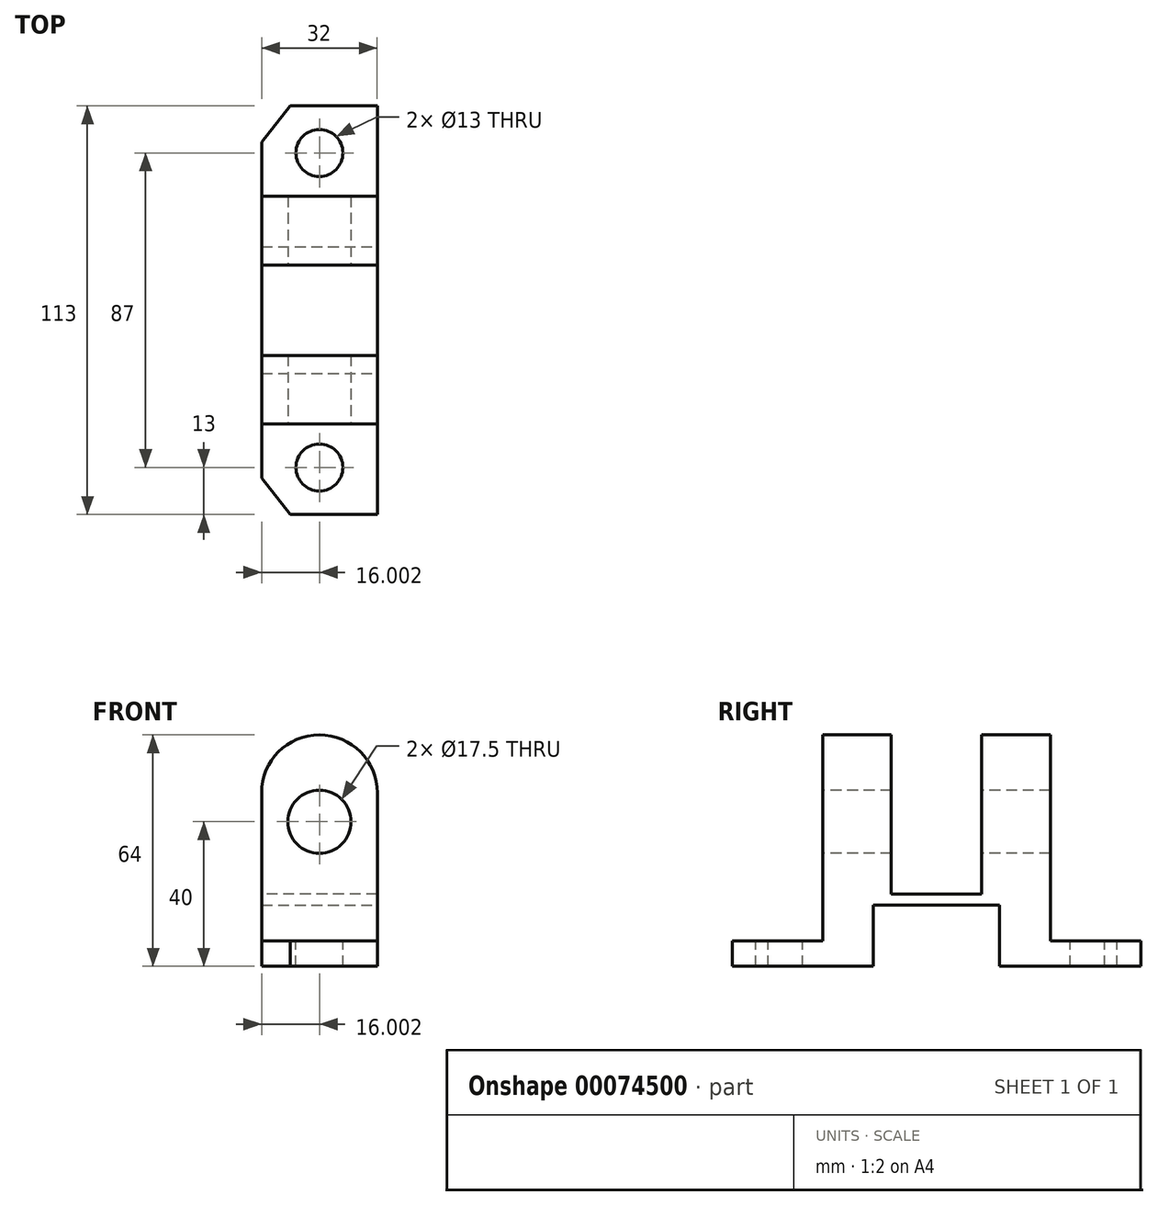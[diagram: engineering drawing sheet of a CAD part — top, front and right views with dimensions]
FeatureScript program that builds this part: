
annotation { "Feature Type Name" : "Feature", "Feature Type Description" : "" }
export const myFeature = defineFeature(function(context is Context, id is Id, definition is map)
    precondition{}
    {
        {
            var Q0;
            Q0=qCreatedBy(makeId("Top.planeOp"),FACE);
            var sketch = newSketch(context, id + "F0", { "sketchPlane" : qUnion([Q0])});
            skLineSegment(sketch, "E0.bottom", {"start": v(-7.48, 89.64) * mm, "end": v(-39.48, 89.64) * mm});
            skLineSegment(sketch, "E0.top", {"start": v(-7.48, -23.36) * mm, "end": v(-39.48, -23.36) * mm});
            skLineSegment(sketch, "E0.left", {"start": v(-7.48, 89.64) * mm, "end": v(-7.48, -23.36) * mm});
            skLineSegment(sketch, "E0.right", {"start": v(-39.48, 89.64) * mm, "end": v(-39.48, -23.36) * mm});
            skSolve(sketch);
        }
        {
            var Q0;
            Q0 = qSketchRegion(id + "F0", true);
            extrude(context, id + "F1", {"entities" : qUnion([Q0]), "depth" : 20 * mm});
        }
        {
            var Q0;
            Q0=makeQuery(id+"F1.opExtrude","CAP_FACE",FACE,{"disambiguationData":[OSD([sQuery(id+"F0.wireOp",EDGE,"E0.bottom"),sQuery(id+"F0.wireOp",EDGE,"E0.top"),sQuery(id+"F0.wireOp",EDGE,"E0.left"),sQuery(id+"F0.wireOp",EDGE,"E0.right")])],"isStart":false});
            var sketch = newSketch(context, id + "F2", { "sketchPlane" : qUnion([Q0])});
            skLineSegment(sketch, "E1.bottom", {"start": v(-39.48, 89.64) * mm, "end": v(-7.48, 89.64) * mm});
            skLineSegment(sketch, "E1.top", {"start": v(-39.48, 64.64) * mm, "end": v(-7.48, 64.64) * mm});
            skLineSegment(sketch, "E1.left", {"start": v(-39.48, 89.64) * mm, "end": v(-39.48, 64.64) * mm});
            skLineSegment(sketch, "E1.right", {"start": v(-7.48, 89.64) * mm, "end": v(-7.48, 64.64) * mm});
            skLineSegment(sketch, "E2.bottom", {"start": v(-7.48, -23.36) * mm, "end": v(-39.48, -23.36) * mm});
            skLineSegment(sketch, "E2.top", {"start": v(-7.48, 1.64) * mm, "end": v(-39.48, 1.64) * mm});
            skLineSegment(sketch, "E2.left", {"start": v(-7.48, -23.36) * mm, "end": v(-7.48, 1.64) * mm});
            skLineSegment(sketch, "E2.right", {"start": v(-39.48, -23.36) * mm, "end": v(-39.48, 1.64) * mm});
            skSolve(sketch);
        }
        {
            var Q0;
            Q0 = qSketchRegion(id + "F2", true);
            extrude(context, id + "F3", {"entities" : qUnion([Q0]), "operationType" : NewBodyOperationType.REMOVE, "oppositeDirection" : true, "depth" : 13 * mm});
        }
        {
            var Q0;
            Q0=makeQuery(id+"F1.opExtrude","CAP_FACE",FACE,{"disambiguationData":[OSD([sQuery(id+"F0.wireOp",EDGE,"E0.bottom"),sQuery(id+"F0.wireOp",EDGE,"E0.top"),sQuery(id+"F0.wireOp",EDGE,"E0.left"),sQuery(id+"F0.wireOp",EDGE,"E0.right")])],"isStart":true});
            var sketch = newSketch(context, id + "F4", { "sketchPlane" : qUnion([Q0])});
            skLineSegment(sketch, "E3", {"start": v(-39.48, -50.64) * mm, "end": v(-39.48, -15.64) * mm});
            skLineSegment(sketch, "E4.bottom", {"start": v(-39.48, -50.64) * mm, "end": v(-7.48, -50.64) * mm});
            skLineSegment(sketch, "E4.top", {"start": v(-39.48, -15.64) * mm, "end": v(-7.48, -15.64) * mm});
            skLineSegment(sketch, "E4.right", {"start": v(-7.48, -50.64) * mm, "end": v(-7.48, -15.64) * mm});
            skSolve(sketch);
        }
        {
            var Q0;
            Q0 = qSketchRegion(id + "F4", true);
            extrude(context, id + "F5", {"entities" : qUnion([Q0]), "operationType" : NewBodyOperationType.REMOVE, "oppositeDirection" : true, "depth" : 17 * mm});
        }
        {
            var Q0;
            Q0=makeQuery(id+"F1.opExtrude","CAP_FACE",FACE,{"disambiguationData":[OSD([sQuery(id+"F0.wireOp",EDGE,"E0.bottom"),sQuery(id+"F0.wireOp",EDGE,"E0.top"),sQuery(id+"F0.wireOp",EDGE,"E0.left"),sQuery(id+"F0.wireOp",EDGE,"E0.right")])],"isStart":false});
            var sketch = newSketch(context, id + "F6", { "sketchPlane" : qUnion([Q0])});
            skLineSegment(sketch, "E5.bottom", {"start": v(-39.48, 64.64) * mm, "end": v(-7.48, 64.64) * mm});
            skLineSegment(sketch, "E5.top", {"start": v(-39.48, 45.64) * mm, "end": v(-7.48, 45.64) * mm});
            skLineSegment(sketch, "E5.left", {"start": v(-39.48, 64.64) * mm, "end": v(-39.48, 45.64) * mm});
            skLineSegment(sketch, "E5.right", {"start": v(-7.48, 64.64) * mm, "end": v(-7.48, 45.64) * mm});
            skLineSegment(sketch, "E6.bottom", {"start": v(-7.48, 1.64) * mm, "end": v(-39.48, 1.64) * mm});
            skLineSegment(sketch, "E6.top", {"start": v(-7.48, 20.64) * mm, "end": v(-39.48, 20.64) * mm});
            skLineSegment(sketch, "E6.left", {"start": v(-7.48, 1.64) * mm, "end": v(-7.48, 20.64) * mm});
            skLineSegment(sketch, "E6.right", {"start": v(-39.48, 1.64) * mm, "end": v(-39.48, 20.64) * mm});
            skSolve(sketch);
        }
        {
            var Q0;
            Q0 = qSketchRegion(id + "F6", true);
            extrude(context, id + "F7", {"entities" : qUnion([Q0]), "operationType" : NewBodyOperationType.ADD, "depth" : 44 * mm});
        }
        {
            var Q0;
            Q0=makeQuery(id+"F7.opExtrude","CAP_EDGE",EDGE,{"disambiguationData":[OSD([sQuery(id+"F6.wireOp",EDGE,"E5.left")])],"isStart":false});
            fillet(context, id + "F8", {"entities" : qUnion([Q0]), "radius" : 16 * mm, "tangentPropagation" : true, "allowEdgeOverflow" : false});
        }
        {
            var Q0;
            Q0=makeQuery(id+"F7.opExtrude","CAP_EDGE",EDGE,{"disambiguationData":[OSD([sQuery(id+"F6.wireOp",EDGE,"E5.right")])],"isStart":false});
            fillet(context, id + "F9", {"entities" : qUnion([Q0]), "radius" : 16 * mm, "tangentPropagation" : true, "allowEdgeOverflow" : false});
        }
        {
            var Q0;
            Q0=makeQuery(id+"F7.opExtrude","CAP_EDGE",EDGE,{"disambiguationData":[OSD([sQuery(id+"F6.wireOp",EDGE,"E6.right")])],"isStart":false});
            fillet(context, id + "F10", {"entities" : qUnion([Q0]), "radius" : 16 * mm, "tangentPropagation" : true, "allowEdgeOverflow" : false});
        }
        {
            var Q0;
            Q0=makeQuery(id+"F7.opExtrude","CAP_EDGE",EDGE,{"disambiguationData":[OSD([sQuery(id+"F6.wireOp",EDGE,"E6.left")])],"isStart":false});
            fillet(context, id + "F11", {"entities" : qUnion([Q0]), "radius" : 16 * mm, "tangentPropagation" : true, "allowEdgeOverflow" : false});
        }
        {
            var Q0;
            Q0=makeQuery(id+"F3.boolean.opBoolean","COPY",FACE,{"derivedFrom":makeQuery(id+"F3.opExtrude","CAP_FACE",FACE,{"disambiguationData":[OSD([sQuery(id+"F2.wireOp",EDGE,"E2.bottom"),sQuery(id+"F2.wireOp",EDGE,"E2.top"),sQuery(id+"F2.wireOp",EDGE,"E2.left"),sQuery(id+"F2.wireOp",EDGE,"E2.right")])],"isStart":false})});
            var sketch = newSketch(context, id + "F12", { "sketchPlane" : qUnion([Q0])});
            skCircle(sketch, "E7", {"center": v(-23.48, -10.36) * mm, "radius": 6.5 * mm});
            skSolve(sketch);
        }
        {
            var Q0;
            Q0 = qSketchRegion(id + "F12", true);
            extrude(context, id + "F13", {"entities" : qUnion([Q0]), "operationType" : NewBodyOperationType.REMOVE, "oppositeDirection" : true, "depth" : 13 * mm});
        }
        {
            var Q0;
            Q0=makeQuery(id+"F3.boolean.opBoolean","COPY",FACE,{"derivedFrom":makeQuery(id+"F3.opExtrude","CAP_FACE",FACE,{"disambiguationData":[OSD([sQuery(id+"F2.wireOp",EDGE,"E1.bottom"),sQuery(id+"F2.wireOp",EDGE,"E1.top"),sQuery(id+"F2.wireOp",EDGE,"E1.left"),sQuery(id+"F2.wireOp",EDGE,"E1.right")])],"isStart":false})});
            var sketch = newSketch(context, id + "F14", { "sketchPlane" : qUnion([Q0])});
            skCircle(sketch, "E8", {"center": v(-23.48, 76.64) * mm, "radius": 6.5 * mm});
            skSolve(sketch);
        }
        {
            var Q0;
            Q0 = qSketchRegion(id + "F14", true);
            extrude(context, id + "F15", {"entities" : qUnion([Q0]), "operationType" : NewBodyOperationType.REMOVE, "oppositeDirection" : true, "depth" : 13 * mm});
        }
        {
            var Q0;
            Q0=makeQuery(id+"F3.boolean.opBoolean","COPY",FACE,{"derivedFrom":makeQuery(id+"F3.opExtrude","CAP_FACE",FACE,{"disambiguationData":[OSD([sQuery(id+"F2.wireOp",EDGE,"E2.bottom"),sQuery(id+"F2.wireOp",EDGE,"E2.top"),sQuery(id+"F2.wireOp",EDGE,"E2.left"),sQuery(id+"F2.wireOp",EDGE,"E2.right")])],"isStart":false})});
            var sketch = newSketch(context, id + "F16", { "sketchPlane" : qUnion([Q0])});
            skLineSegment(sketch, "E9", {"start": v(-39.48, -23.36) * mm, "end": v(-39.48, -13.36) * mm});
            skPoint(sketch, "E10.endSnap0", {"position": v(-39.48, -18.36) * mm});
            skLineSegment(sketch, "E11", {"start": v(-39.48, -23.36) * mm, "end": v(-31.48, -23.36) * mm});
            skLineSegment(sketch, "E12", {"start": v(-39.48, -13.36) * mm, "end": v(-31.48, -23.36) * mm});
            skSolve(sketch);
        }
        {
            var Q0;
            Q0 = qSketchRegion(id + "F16", true);
            extrude(context, id + "F17", {"entities" : qUnion([Q0]), "operationType" : NewBodyOperationType.REMOVE, "oppositeDirection" : true, "depth" : 25 * mm});
        }
        {
            var Q0;
            Q0=makeQuery(id+"F3.boolean.opBoolean","COPY",FACE,{"derivedFrom":makeQuery(id+"F3.opExtrude","CAP_FACE",FACE,{"disambiguationData":[OSD([sQuery(id+"F2.wireOp",EDGE,"E1.bottom"),sQuery(id+"F2.wireOp",EDGE,"E1.top"),sQuery(id+"F2.wireOp",EDGE,"E1.left"),sQuery(id+"F2.wireOp",EDGE,"E1.right")])],"isStart":false})});
            var sketch = newSketch(context, id + "F18", { "sketchPlane" : qUnion([Q0])});
            skLineSegment(sketch, "E13", {"start": v(-39.48, 89.64) * mm, "end": v(-31.48, 89.64) * mm});
            skLineSegment(sketch, "E14", {"start": v(-39.48, 89.64) * mm, "end": v(-39.48, 79.64) * mm});
            skLineSegment(sketch, "E15", {"start": v(-31.48, 89.64) * mm, "end": v(-39.48, 79.64) * mm});
            skSolve(sketch);
        }
        {
            var Q0;
            Q0 = qSketchRegion(id + "F18", true);
            extrude(context, id + "F19", {"entities" : qUnion([Q0]), "operationType" : NewBodyOperationType.REMOVE, "oppositeDirection" : true, "depth" : 25 * mm});
        }
        {
            var Q0;
            Q0=makeQuery(id+"F7.boolean.opBoolean","MERGE",FACE,{"derivedFrom":[makeQuery(id+"F3.boolean.opBoolean","COPY",FACE,{"derivedFrom":makeQuery(id+"F3.opExtrude","SWEPT_FACE",FACE,{"disambiguationData":[OSD([sQuery(id+"F2.wireOp",EDGE,"E2.top")])]})}),makeQuery(id+"F7.opExtrude","SWEPT_FACE",FACE,{"disambiguationData":[OSD([sQuery(id+"F6.wireOp",EDGE,"E6.bottom")])]})]});
            var sketch = newSketch(context, id + "F20", { "sketchPlane" : qUnion([Q0])});
            skCircle(sketch, "E16", {"center": v(-23.48, 40) * mm, "radius": 8.75 * mm});
            skSolve(sketch);
        }
        {
            var Q0;
            Q0 = qSketchRegion(id + "F20", true);
            extrude(context, id + "F21", {"entities" : qUnion([Q0]), "operationType" : NewBodyOperationType.REMOVE, "oppositeDirection" : true, "depth" : 100 * mm});
        }
    });
